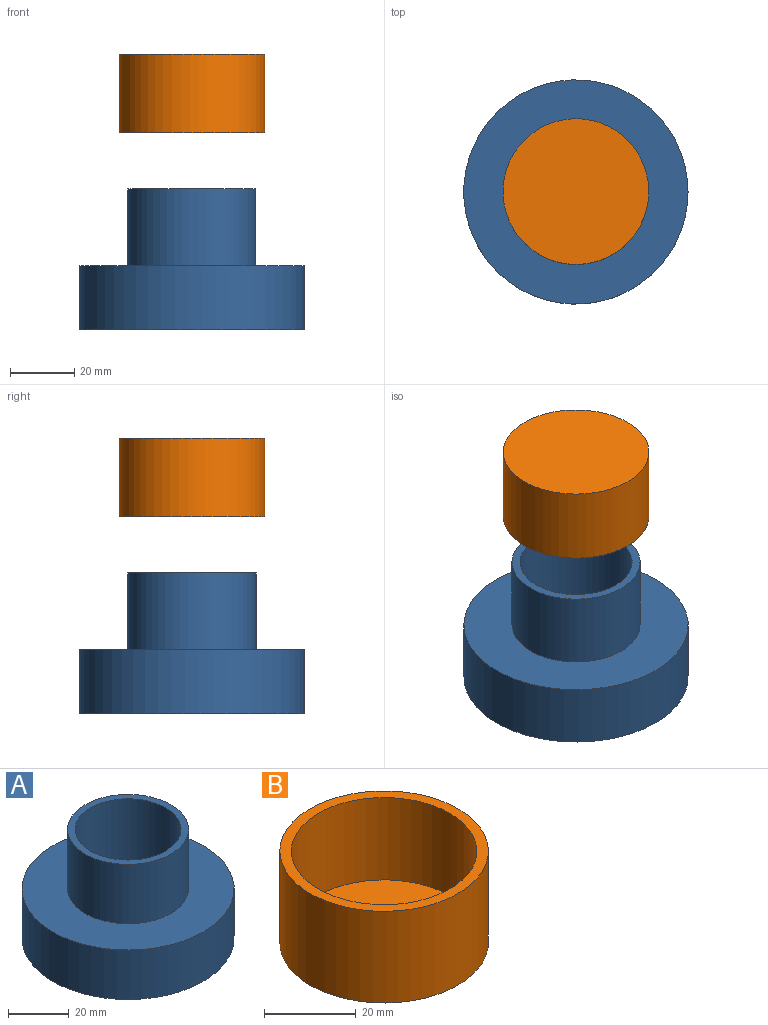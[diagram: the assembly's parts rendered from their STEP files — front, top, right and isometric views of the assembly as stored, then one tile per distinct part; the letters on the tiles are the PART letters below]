
ASSEMBLY  parts=2 mates=1
PART A: 7 faces, bbox 70x70x44 mm
  f0: cylinder r=20mm len=40mm, axis (0,0,-1), area 3015.9mm2, adj f1,f4
  f1: plane 40x40mm, normal (0,0,1), area 294.5mm2, adj f0,f2
  f2: cylinder r=17.5mm len=42mm, axis (0,0,-1), area 4618.1mm2, adj f1,f6
  f3: cylinder r=35mm len=70mm, axis (0,0,-1), area 4398.2mm2, adj f4,f5
  f4: plane 70x70mm, normal (0,0,1), area 2591.8mm2, adj f0,f3
  f5: plane 70x70mm, normal (0,0,-1), area 3848.5mm2, adj f3
  f6: plane 35x35mm, normal (0,0,1), area 962.1mm2, adj f2
PART B: 5 faces, bbox 45.5x45.5x24.5 mm
  f0: cylinder r=22.75mm len=45.5mm, axis (0,0,-1), area 3502.1mm2, adj f1,f2
  f1: plane 45.5x45.5mm, normal (0,0,1), area 337.7mm2, adj f0,f3
  f2: plane 45.5x45.5mm, normal (0,0,-1), area 1626mm2, adj f0
  f3: cylinder r=20.25mm len=40.5mm, axis (0,0,-1), area 2799.2mm2, adj f1,f4
  f4: plane 40.5x40.5mm, normal (0,0,1), area 1288.2mm2, adj f3
PLACE A t=(-42.09,-26.97,130.06)mm
PLACE B rot(axis=(-1,0,0),180deg) t=(-42.09,-26.97,216.18)mm
MATE slider A.f0 <-> B.f0  axis (0,0,-1) through (-42.09,-26.97,174.06)mm
